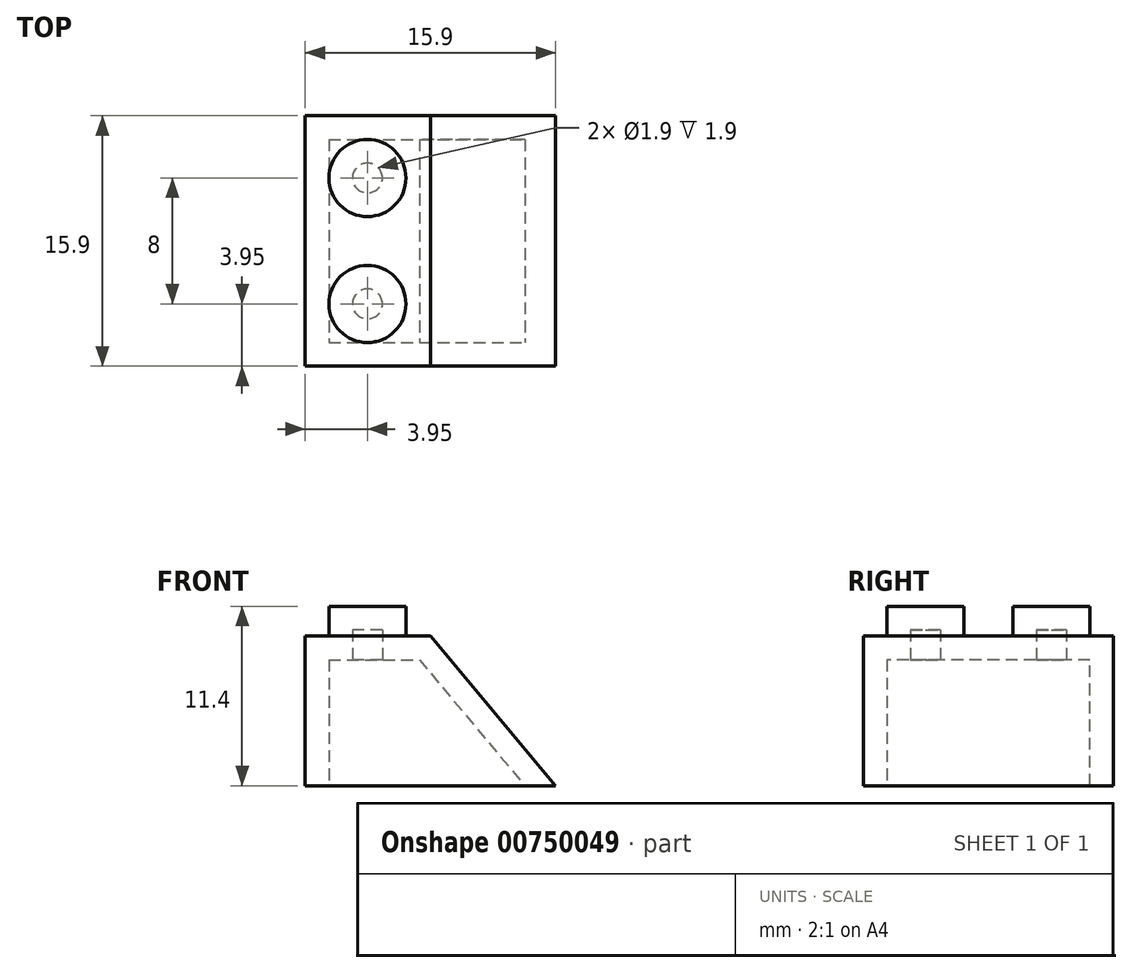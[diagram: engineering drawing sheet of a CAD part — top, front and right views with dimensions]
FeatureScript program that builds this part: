
annotation { "Feature Type Name" : "Feature", "Feature Type Description" : "" }
export const myFeature = defineFeature(function(context is Context, id is Id, definition is map)
    precondition{}
    {
        {
            var Q0;
            Q0=qCreatedBy(makeId("Top.planeOp"),FACE);
            var sketch = newSketch(context, id + "F0", { "sketchPlane" : qUnion([Q0])});
            skLineSegment(sketch, "E0.bottom", {"start": v(0, 0) * mm, "end": v(15.9, 0) * mm});
            skLineSegment(sketch, "E0.top", {"start": v(0, -15.9) * mm, "end": v(15.9, -15.9) * mm});
            skLineSegment(sketch, "E0.left", {"start": v(0, 0) * mm, "end": v(0, -15.9) * mm});
            skLineSegment(sketch, "E0.right", {"start": v(15.9, 0) * mm, "end": v(15.9, -15.9) * mm});
            skCircle(sketch, "E1", {"center": v(3.95, -3.95) * mm, "radius": 2.45 * mm});
            skCircle(sketch, "E2", {"center": v(3.95, -11.95) * mm, "radius": 2.45 * mm});
            skSolve(sketch);
        }
        {
            var Q0;
            Q0 = qSketchRegion(id + "F0", true);
            extrude(context, id + "F1", {"entities" : qUnion([Q0]), "depth" : 9.5 * mm, "offsetDistance" : 25 * mm});
        }
        {
            var Q0;
            Q0=makeQuery(id+"F0.imprint","IMPRINT",FACE,{"disambiguationData":[TD([[makeQuery(id+"F0.imprint","IMPRINT",EDGE,{"derivedFrom":sQuery(id+"F0.wireOp",EDGE,"E1")}),1.0]])]});
            var Q1;
            Q1=makeQuery(id+"F0.imprint","IMPRINT",FACE,{"disambiguationData":[TD([[makeQuery(id+"F0.imprint","IMPRINT",EDGE,{"derivedFrom":sQuery(id+"F0.wireOp",EDGE,"E2")}),1.0]])]});
            extrude(context, id + "F2", {"entities" : qUnion([Q0, Q1]), "operationType" : NewBodyOperationType.ADD, "depth" : 11.4 * mm, "offsetDistance" : 25 * mm});
        }
        {
            var Q0;
            Q0=makeQuery(id+"F0.imprint","IMPRINT",FACE,{"disambiguationData":[TD([[makeQuery(id+"F0.imprint","IMPRINT",EDGE,{"derivedFrom":sQuery(id+"F0.wireOp",EDGE,"E0.bottom")}),-1.0]])]});
            var sketch = newSketch(context, id + "F3", { "sketchPlane" : qUnion([Q0])});
            skLineSegment(sketch, "E3.0", {"start": v(1.5, -1.5) * mm, "end": v(1.5, -14.4) * mm});
            skLineSegment(sketch, "E3.1", {"start": v(1.5, -1.5) * mm, "end": v(14.4, -1.5) * mm});
            skLineSegment(sketch, "E3.2", {"start": v(14.4, -1.5) * mm, "end": v(14.4, -14.4) * mm});
            skLineSegment(sketch, "E3.3", {"start": v(1.5, -14.4) * mm, "end": v(14.4, -14.4) * mm});
            skCircle(sketch, "E4", {"center": v(7.95, -7.95) * mm, "radius": 3.23 * mm});
            skPoint(sketch, "E4.centerSnap0", {"position": v(1.5, -7.95) * mm});
            skPoint(sketch, "E4.centerSnap1", {"position": v(7.95, -14.4) * mm});
            skCircle(sketch, "E5", {"center": v(7.95, -7.95) * mm, "radius": 2.73 * mm});
            skSolve(sketch);
        }
        {
            var Q0;
            Q0=makeQuery(id+"F1.opExtrude","SWEPT_FACE",FACE,{"disambiguationData":[OSD([sQuery(id+"F0.wireOp",EDGE,"E0.top")])]});
            var sketch = newSketch(context, id + "F4", { "sketchPlane" : qUnion([Q0])});
            skPoint(sketch, "E6", {"position": v(7.95, 9.5) * mm});
            skLineSegment(sketch, "E7", {"start": v(7.95, 9.5) * mm, "end": v(15.9, 0) * mm});
            skSolve(sketch);
        }
        {
            var Q0;
            Q0=makeQuery(id+"F3.imprint","IMPRINT",FACE,{"disambiguationData":[TD([[makeQuery(id+"F3.imprint","IMPRINT",EDGE,{"derivedFrom":sQuery(id+"F3.wireOp",EDGE,"E5")}),-1.0]])]});
            extrude(context, id + "F5", {"entities" : qUnion([Q0]), "operationType" : NewBodyOperationType.ADD, "depth" : 9.5 * mm, "offsetDistance" : 25 * mm});
        }
        {
            var Q0;
            {var subQ0=sQuery(id+"F4.wireOp",EDGE,"E7");Q0=makeQuery(id+"F4.imprint","IMPRINT",FACE,{"disambiguationData":[TD([[makeQuery(id+"F4.imprint","IMPRINT",EDGE,{"derivedFrom":subQ0}),1.0]])]});}
            extrude(context, id + "F6", {"entities" : qUnion([Q0]), "operationType" : NewBodyOperationType.REMOVE, "oppositeDirection" : true, "depth" : 25 * mm, "offsetDistance" : 25 * mm});
        }
        {
            var Q0;
            {var subQ0=sQuery(id+"F0.wireOp",EDGE,"E2");var subQ1=sQuery(id+"F0.wireOp",EDGE,"E1");Q0=makeQuery(id+"F2.boolean.opBoolean","MERGE",FACE,{"derivedFrom":[makeQuery(id+"F1.opExtrude","CAP_FACE",FACE,{"disambiguationData":[OSD([sQuery(id+"F0.wireOp",EDGE,"E0.bottom"),sQuery(id+"F0.wireOp",EDGE,"E0.top"),sQuery(id+"F0.wireOp",EDGE,"E0.left"),sQuery(id+"F0.wireOp",EDGE,"E0.right"),subQ1,subQ0])],"isStart":true}),makeQuery(id+"F2.opExtrude","CAP_FACE",FACE,{"disambiguationData":[OSD([subQ1])],"isStart":true}),makeQuery(id+"F2.opExtrude","CAP_FACE",FACE,{"disambiguationData":[OSD([subQ0])],"isStart":true})]});}
            shell(context, id + "F7", {"entities" : qUnion([Q0]), "thickness" : 1.5 * mm});
        }
    });
